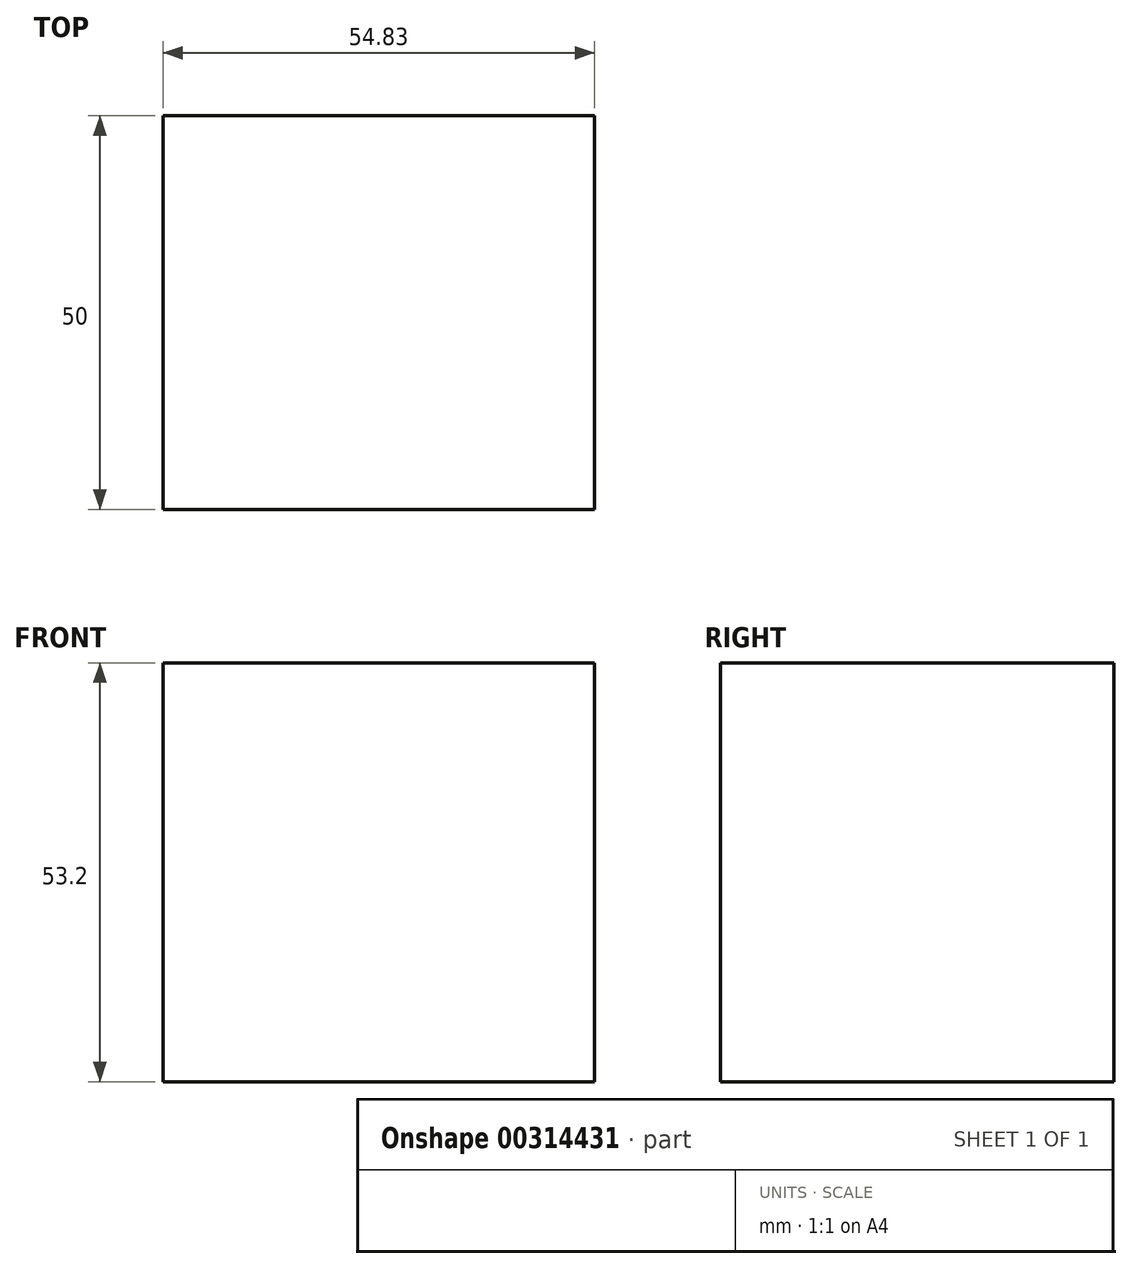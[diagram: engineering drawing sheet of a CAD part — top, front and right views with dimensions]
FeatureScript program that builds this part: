
annotation { "Feature Type Name" : "Feature", "Feature Type Description" : "" }
export const myFeature = defineFeature(function(context is Context, id is Id, definition is map)
    precondition{}
    {
        {
            var Q0;
            Q0=qCreatedBy(makeId("Front.planeOp"),FACE);
            var sketch = newSketch(context, id + "F0", { "sketchPlane" : qUnion([Q0])});
            skLineSegment(sketch, "E0.bottom", {"start": v(150, -80) * mm, "end": v(-150, -80) * mm});
            skLineSegment(sketch, "E0.top", {"start": v(150, 80) * mm, "end": v(-150, 80) * mm});
            skLineSegment(sketch, "E0.left", {"start": v(150, -80) * mm, "end": v(150, 80) * mm});
            skLineSegment(sketch, "E0.right", {"start": v(-150, -80) * mm, "end": v(-150, 80) * mm});
            skPoint(sketch, "E0.middle", {"position": v(0, 0) * mm});
            skLineSegment(sketch, "E1.bottom", {"start": v(150, -80) * mm, "end": v(95.17, -80) * mm});
            skLineSegment(sketch, "E1.top", {"start": v(150, -26.8) * mm, "end": v(95.17, -26.8) * mm});
            skLineSegment(sketch, "E1.left", {"start": v(150, -80) * mm, "end": v(150, -26.8) * mm});
            skLineSegment(sketch, "E1.right", {"start": v(95.17, -80) * mm, "end": v(95.17, -26.8) * mm});
            skSolve(sketch);
        }
        {
            var Q0;
            Q0=makeQuery(id+"F0.imprint","IMPRINT",FACE,{"disambiguationData":[TD([[makeQuery(id+"F0.imprint","IMPRINT",EDGE,{"derivedFrom":sQuery(id+"F0.wireOp",EDGE,"E0.bottom")}),-1.0]])]});
            extrude(context, id + "F1", {"entities" : qUnion([Q0]), "depth" : 50 * mm, "offsetDistance" : 25 * mm});
        }
        {
            var Q0;
            Q0=qCreatedBy(makeId("Front.planeOp"),FACE);
            var sketch = newSketch(context, id + "F2", { "sketchPlane" : qUnion([Q0])});
            skCircle(sketch, "E2", {"center": v(0, 0) * mm, "radius": 22.25 * mm});
            skSolve(sketch);
        }
        {
            var Q0;
            Q0=makeQuery(id+"F2.imprint","IMPRINT",FACE,{"disambiguationData":[TD([[makeQuery(id+"F2.imprint","IMPRINT",EDGE,{"derivedFrom":sQuery(id+"F2.wireOp",EDGE,"E2")}),1.0]])]});
            extrude(context, id + "F3", {"entities" : qUnion([Q0]), "operationType" : NewBodyOperationType.REMOVE, "endBound" : BoundingType.THROUGH_ALL, "depth" : 25 * mm, "offsetDistance" : 25 * mm});
        }
    });
